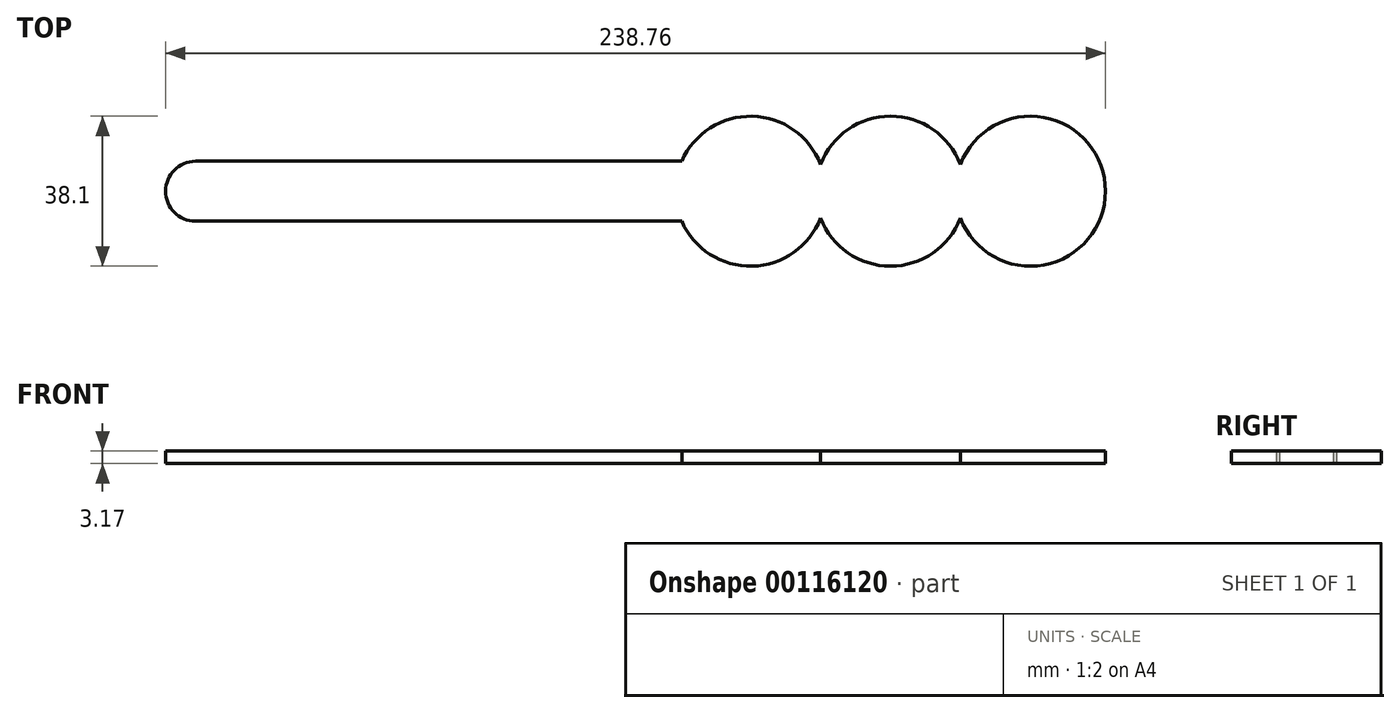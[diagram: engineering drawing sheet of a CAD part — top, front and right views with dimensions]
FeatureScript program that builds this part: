
annotation { "Feature Type Name" : "Feature", "Feature Type Description" : "" }
export const myFeature = defineFeature(function(context is Context, id is Id, definition is map)
    precondition{}
    {
        {
            var Q0;
            Q0=qCreatedBy(makeId("Top.planeOp"),FACE);
            var sketch = newSketch(context, id + "F0", { "sketchPlane" : qUnion([Q0])});
            skPoint(sketch, "E0.visualSharp", {"position": v(0, 15.24) * mm});
            skPoint(sketch, "E1.visualSharp", {"position": v(0, 0) * mm});
            skArc(sketch, "E2", {"start": v(201.93, 0.78) * mm, "mid": v(238.76, 7.62) * mm, "end": v(201.93, 14.46) * mm});
            skPoint(sketch, "E0.filletArc.start.orphan", {"position": v(6.35, 15.24) * mm});
            skLineSegment(sketch, "E3.bottom", {"start": v(7.62, 0) * mm, "end": v(131.13, 0) * mm});
            skLineSegment(sketch, "E3.top", {"start": v(7.62, 15.24) * mm, "end": v(131.13, 15.24) * mm});
            skLineSegment(sketch, "E3.left", {"start": v(0, 7.62) * mm, "end": v(0, 7.62) * mm});
            skArc(sketch, "E4", {"start": v(166.37, 0.78) * mm, "mid": v(184.15, -11.43) * mm, "end": v(201.93, 0.78) * mm});
            skArc(sketch, "E5", {"start": v(131.13, 0) * mm, "mid": v(149.01, -11.43) * mm, "end": v(166.37, 0.78) * mm});
            skArc(sketch, "E6.filletArc", {"start": v(7.62, 15.24) * mm, "mid": v(2.23, 13) * mm, "end": v(0, 7.62) * mm});
            skArc(sketch, "E7.filletArc", {"start": v(0, 7.62) * mm, "mid": v(2.23, 2.23) * mm, "end": v(7.62, 0) * mm});
            skLineSegment(sketch, "E8.trimOffspring", {"start": v(166.05, 15.24) * mm, "end": v(166.7, 15.24) * mm});
            skLineSegment(sketch, "E9.trimOffspring", {"start": v(166.05, 0) * mm, "end": v(166.7, 0) * mm});
            skArc(sketch, "E10.trimOffspring", {"start": v(166.37, 14.46) * mm, "mid": v(149.01, 26.67) * mm, "end": v(131.13, 15.24) * mm});
            skLineSegment(sketch, "E11.trimOffspring", {"start": v(201.6, 15.24) * mm, "end": v(202.25, 15.24) * mm});
            skLineSegment(sketch, "E12.trimOffspring", {"start": v(201.6, 0) * mm, "end": v(202.25, 0) * mm});
            skArc(sketch, "E13.trimOffspring", {"start": v(201.93, 14.46) * mm, "mid": v(184.15, 26.67) * mm, "end": v(166.37, 14.46) * mm});
            skPoint(sketch, "E14.trimOffspring.end.orphan", {"position": v(238.76, 15.24) * mm});
            skPoint(sketch, "E15.trimOffspring.end.orphan", {"position": v(238.76, 0) * mm});
            skSolve(sketch);
        }
        {
            var Q0;
            {var subQ11=sQuery(id+"F0.wireOp",EDGE,"E3.bottom");Q0=makeQuery(id+"F0.imprint","IMPRINT",FACE,{"disambiguationData":[TD([[makeQuery(id+"F0.imprint","IMPRINT",EDGE,{"derivedFrom":subQ11}),1.0]])]});}
            extrude(context, id + "F1", {"entities" : qUnion([Q0]), "depth" : 3.17 * mm});
        }
    });
